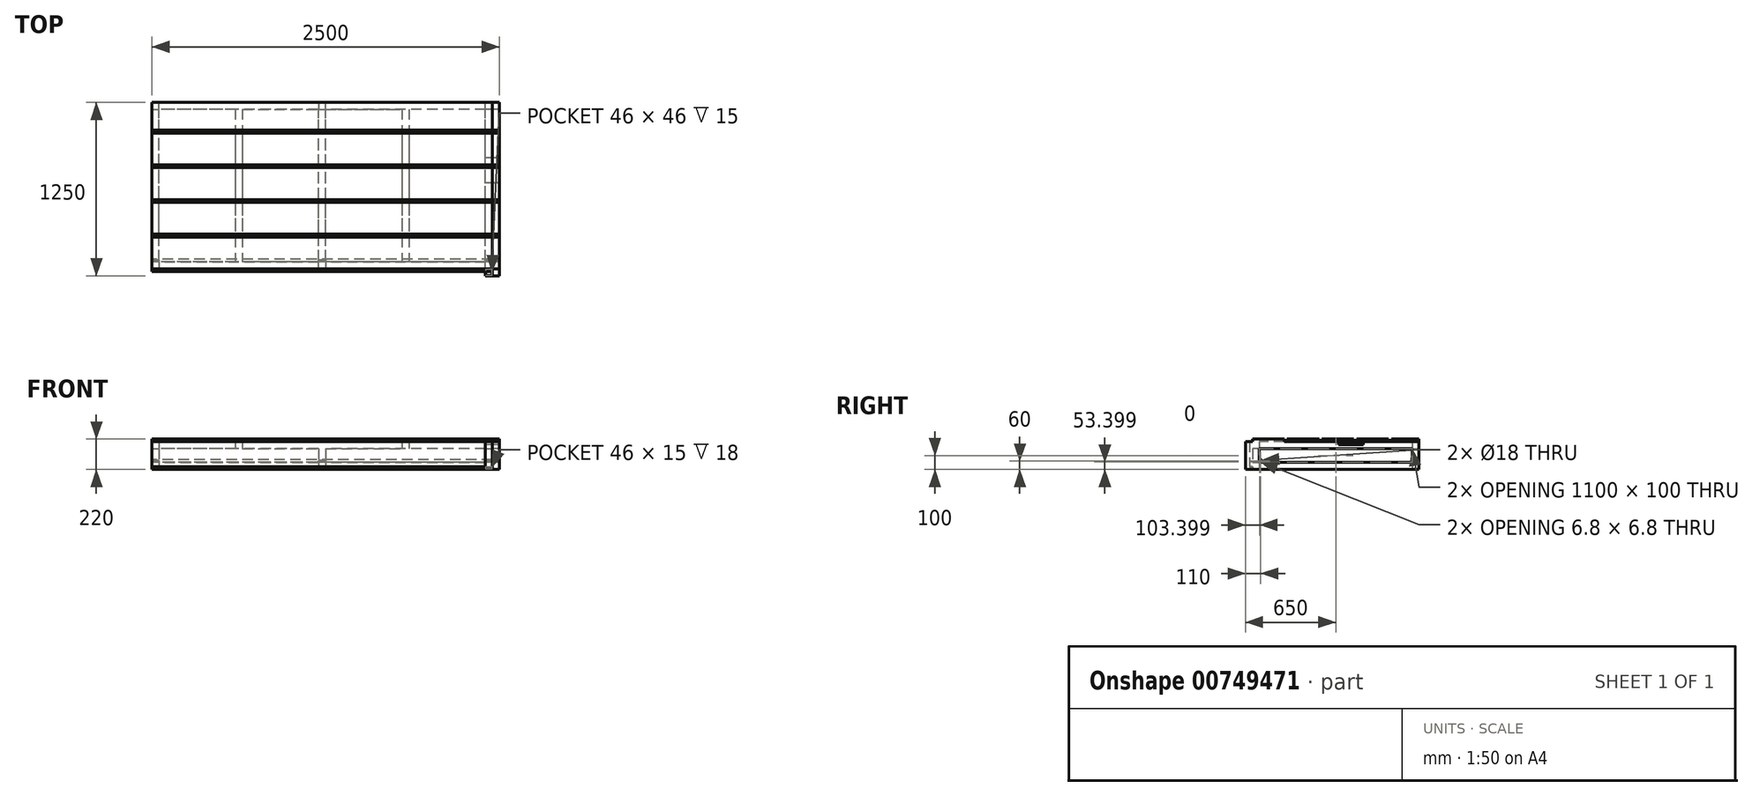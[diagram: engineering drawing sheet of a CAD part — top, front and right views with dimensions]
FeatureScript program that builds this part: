
annotation { "Feature Type Name" : "Feature", "Feature Type Description" : "" }
export const myFeature = defineFeature(function(context is Context, id is Id, definition is map)
    precondition{}
    {
        {
            var Q0;
            Q0=qCreatedBy(makeId("Top.planeOp"),FACE);
            var sketch = newSketch(context, id + "F0", { "sketchPlane" : qUnion([Q0])});
            skLineSegment(sketch, "E0.bottom", {"start": v(1225, -600) * mm, "end": v(-1225, -600) * mm});
            skLineSegment(sketch, "E0.top", {"start": v(1225, 600) * mm, "end": v(-1225, 600) * mm});
            skLineSegment(sketch, "E0.left", {"start": v(1225, -600) * mm, "end": v(1225, 600) * mm});
            skLineSegment(sketch, "E0.right", {"start": v(-1225, -600) * mm, "end": v(-1225, 600) * mm});
            skPoint(sketch, "E0.middle", {"position": v(0, 0) * mm});
            skLineSegment(sketch, "E1.0", {"start": v(1225, 550) * mm, "end": v(-1225, 550) * mm});
            skLineSegment(sketch, "E2.0", {"start": v(1227.5, -600) * mm, "end": v(1227.5, 600) * mm});
            skLineSegment(sketch, "E3.0", {"start": v(1175, -600) * mm, "end": v(1175, 600) * mm});
            skLineSegment(sketch, "E4.0", {"start": v(1225, -550) * mm, "end": v(-1225, -550) * mm});
            skLineSegment(sketch, "E5.0", {"start": v(-1175, -600) * mm, "end": v(-1175, 600) * mm});
            skLineSegment(sketch, "E6", {"start": v(0, 0) * mm, "end": v(0, 550) * mm});
            skLineSegment(sketch, "E7", {"start": v(0, 0) * mm, "end": v(0, -550) * mm});
            skLineSegment(sketch, "E8.0", {"start": v(25, 0) * mm, "end": v(25, 550) * mm});
            skLineSegment(sketch, "E9.0", {"start": v(-25, 0) * mm, "end": v(-25, 550) * mm});
            skLineSegment(sketch, "E10.0", {"start": v(-25, 0) * mm, "end": v(-25, -550) * mm});
            skLineSegment(sketch, "E11.0", {"start": v(25, 0) * mm, "end": v(25, -550) * mm});
            skSolve(sketch);
        }
        {
            var Q0;
            Q0=qSketchRegion(id+"F0",true);
            var Q1;
            {var subQ1=sQuery(id+"F0.wireOp",EDGE,"E6");Q1=makeQuery(id+"F0.imprint","IMPRINT",FACE,{"disambiguationData":[TD([[makeQuery(id+"F0.imprint","IMPRINT",EDGE,{"derivedFrom":subQ1}),-1.0]])]});}
            var Q2;
            {var subQ3=sQuery(id+"F0.wireOp",EDGE,"E6");Q2=makeQuery(id+"F0.imprint","IMPRINT",FACE,{"disambiguationData":[TD([[makeQuery(id+"F0.imprint","IMPRINT",EDGE,{"derivedFrom":subQ3}),1.0]])]});}
            extrude(context, id + "F1", {"entities" : qUnion([Q0, Q1, Q2]), "depth" : 50 * mm, "offsetDistance" : 25 * mm});
        }
        {
            var Q0;
            Q0=makeQuery(id+"F1.opExtrude","CAP_FACE",FACE,{"disambiguationData":[OSD([sQuery(id+"F0.wireOp",EDGE,"E0.bottom"),sQuery(id+"F0.wireOp",EDGE,"E0.top"),sQuery(id+"F0.wireOp",EDGE,"E0.left"),sQuery(id+"F0.wireOp",EDGE,"E0.right"),sQuery(id+"F0.wireOp",EDGE,"E1.0"),sQuery(id+"F0.wireOp",EDGE,"E3.0"),sQuery(id+"F0.wireOp",EDGE,"E4.0"),sQuery(id+"F0.wireOp",EDGE,"E5.0"),sQuery(id+"F0.wireOp",EDGE,"E8.0"),sQuery(id+"F0.wireOp",EDGE,"E9.0"),sQuery(id+"F0.wireOp",EDGE,"E10.0"),sQuery(id+"F0.wireOp",EDGE,"E11.0")])],"isStart":false});
            var sketch = newSketch(context, id + "F2", { "sketchPlane" : qUnion([Q0])});
            skLineSegment(sketch, "E12", {"start": v(-25, 550) * mm, "end": v(25, 550) * mm});
            skLineSegment(sketch, "E13", {"start": v(25, 550) * mm, "end": v(25, 600) * mm});
            skLineSegment(sketch, "E14", {"start": v(25, 600) * mm, "end": v(-25, 600) * mm});
            skLineSegment(sketch, "E15", {"start": v(-25, 600) * mm, "end": v(-25, 550) * mm});
            skLineSegment(sketch, "E16", {"start": v(-1175, 550) * mm, "end": v(-1175, 600) * mm});
            skLineSegment(sketch, "E17", {"start": v(-1175, 600) * mm, "end": v(-1225, 600) * mm});
            skLineSegment(sketch, "E18", {"start": v(-1225, 600) * mm, "end": v(-1225, 550) * mm});
            skLineSegment(sketch, "E19", {"start": v(-1225, 550) * mm, "end": v(-1175, 550) * mm});
            skLineSegment(sketch, "E20", {"start": v(-1175, -550) * mm, "end": v(-1175, -600) * mm});
            skLineSegment(sketch, "E21", {"start": v(-1175, -600) * mm, "end": v(-1225, -600) * mm});
            skLineSegment(sketch, "E22", {"start": v(-1225, -600) * mm, "end": v(-1225, -550) * mm});
            skLineSegment(sketch, "E23", {"start": v(-1225, -550) * mm, "end": v(-1175, -550) * mm});
            skLineSegment(sketch, "E24", {"start": v(-25, -550) * mm, "end": v(25, -550) * mm});
            skLineSegment(sketch, "E25", {"start": v(25, -550) * mm, "end": v(25, -600) * mm});
            skLineSegment(sketch, "E26", {"start": v(25, -600) * mm, "end": v(-25, -600) * mm});
            skPoint(sketch, "E26.endSnap0", {"position": v(0, -600) * mm});
            skLineSegment(sketch, "E27", {"start": v(-25, -600) * mm, "end": v(-25, -550) * mm});
            skLineSegment(sketch, "E28", {"start": v(1175, -550) * mm, "end": v(1225, -550) * mm});
            skLineSegment(sketch, "E29", {"start": v(1225, -550) * mm, "end": v(1225, -600) * mm});
            skLineSegment(sketch, "E30", {"start": v(1225, -600) * mm, "end": v(1175, -600) * mm});
            skLineSegment(sketch, "E31", {"start": v(1175, -600) * mm, "end": v(1175, -550) * mm});
            skLineSegment(sketch, "E32", {"start": v(1175, 550) * mm, "end": v(1175, 600) * mm});
            skLineSegment(sketch, "E33", {"start": v(1175, 600) * mm, "end": v(1225, 600) * mm});
            skLineSegment(sketch, "E34", {"start": v(1225, 600) * mm, "end": v(1225, 550) * mm});
            skLineSegment(sketch, "E35", {"start": v(1225, 550) * mm, "end": v(1175, 550) * mm});
            skSolve(sketch);
        }
        {
            var Q0;
            Q0=qSketchRegion(id+"F2",true);
            extrude(context, id + "F3", {"entities" : qUnion([Q0]), "operationType" : NewBodyOperationType.ADD, "depth" : 100 * mm, "offsetDistance" : 25 * mm});
        }
        {
            var Q0;
            Q0=makeQuery(id+"F3.opExtrude","CAP_FACE",FACE,{"disambiguationData":[OSD([sQuery(id+"F2.wireOp",EDGE,"E12"),sQuery(id+"F2.wireOp",EDGE,"E13"),sQuery(id+"F2.wireOp",EDGE,"E14"),sQuery(id+"F2.wireOp",EDGE,"E15")])],"isStart":false});
            var sketch = newSketch(context, id + "F4", { "sketchPlane" : qUnion([Q0])});
            skLineSegment(sketch, "E36.bottom", {"start": v(-1225, 600) * mm, "end": v(1225, 600) * mm});
            skLineSegment(sketch, "E36.top", {"start": v(-1225, -600) * mm, "end": v(1225, -600) * mm});
            skLineSegment(sketch, "E36.left", {"start": v(-1225, 600) * mm, "end": v(-1225, -600) * mm});
            skLineSegment(sketch, "E36.right", {"start": v(1225, 600) * mm, "end": v(1225, -600) * mm});
            skLineSegment(sketch, "E37.bottom", {"start": v(1175, -550) * mm, "end": v(-1175, -550) * mm});
            skLineSegment(sketch, "E37.top", {"start": v(1175, 550) * mm, "end": v(-1175, 550) * mm});
            skLineSegment(sketch, "E37.left", {"start": v(1175, -550) * mm, "end": v(1175, 550) * mm});
            skLineSegment(sketch, "E37.right", {"start": v(-1175, -550) * mm, "end": v(-1175, 550) * mm});
            skLineSegment(sketch, "E38.bottom", {"start": v(-25, 550) * mm, "end": v(25, 550) * mm});
            skLineSegment(sketch, "E38.top", {"start": v(-25, -550) * mm, "end": v(25, -550) * mm});
            skLineSegment(sketch, "E38.left", {"start": v(-25, 550) * mm, "end": v(-25, -550) * mm});
            skLineSegment(sketch, "E38.right", {"start": v(25, 550) * mm, "end": v(25, -550) * mm});
            skLineSegment(sketch, "E39", {"start": v(-25, 550) * mm, "end": v(-1175, 550) * mm});
            skLineSegment(sketch, "E40", {"start": v(-600, 550) * mm, "end": v(-600, -550) * mm});
            skLineSegment(sketch, "E41.0", {"start": v(-625, 550) * mm, "end": v(-625, -550) * mm});
            skLineSegment(sketch, "E42.0", {"start": v(-575, 550) * mm, "end": v(-575, -550) * mm});
            skLineSegment(sketch, "E43", {"start": v(25, 550) * mm, "end": v(1175, 550) * mm});
            skLineSegment(sketch, "E44", {"start": v(600, 550) * mm, "end": v(600, -550) * mm});
            skLineSegment(sketch, "E45.0", {"start": v(575, 550) * mm, "end": v(575, -550) * mm});
            skLineSegment(sketch, "E46.0", {"start": v(625, 550) * mm, "end": v(625, -550) * mm});
            skSolve(sketch);
        }
        {
            var Q0;
            Q0=qSketchRegion(id+"F4",true);
            var Q1;
            {var subQ0=sQuery(id+"F4.wireOp",EDGE,"E40");Q1=makeQuery(id+"F4.imprint","IMPRINT",FACE,{"disambiguationData":[TD([[makeQuery(id+"F4.imprint","IMPRINT",EDGE,{"derivedFrom":subQ0}),1.0]])]});}
            var Q2;
            {var subQ0=sQuery(id+"F4.wireOp",EDGE,"E40");Q2=makeQuery(id+"F4.imprint","IMPRINT",FACE,{"disambiguationData":[TD([[makeQuery(id+"F4.imprint","IMPRINT",EDGE,{"derivedFrom":subQ0}),-1.0]])]});}
            var Q3;
            {var subQ0=sQuery(id+"F4.wireOp",EDGE,"E44");Q3=makeQuery(id+"F4.imprint","IMPRINT",FACE,{"disambiguationData":[TD([[makeQuery(id+"F4.imprint","IMPRINT",EDGE,{"derivedFrom":subQ0}),1.0]])]});}
            var Q4;
            {var subQ0=sQuery(id+"F4.wireOp",EDGE,"E44");Q4=makeQuery(id+"F4.imprint","IMPRINT",FACE,{"disambiguationData":[TD([[makeQuery(id+"F4.imprint","IMPRINT",EDGE,{"derivedFrom":subQ0}),-1.0]])]});}
            var Q5;
            Q5=makeQuery(id+"F4.imprint","IMPRINT",FACE,{"disambiguationData":[TD([[makeQuery(id+"F4.imprint","IMPRINT",EDGE,{"derivedFrom":sQuery(id+"F4.wireOp",EDGE,"E38.bottom")}),-1.0]])]});
            extrude(context, id + "F5", {"entities" : qUnion([Q0, Q1, Q2, Q3, Q4, Q5]), "operationType" : NewBodyOperationType.ADD, "depth" : 50 * mm, "offsetDistance" : 25 * mm});
        }
        {
            var Q0;
            Q0=makeQuery(id+"F5.boolean.opBoolean","MERGE",FACE,{"derivedFrom":[makeQuery(id+"F3.boolean.opBoolean","MERGE",FACE,{"derivedFrom":[makeQuery(id+"F1.opExtrude","SWEPT_FACE",FACE,{"disambiguationData":[OSD([sQuery(id+"F0.wireOp",EDGE,"E0.right")])]}),makeQuery(id+"F3.opExtrude","SWEPT_FACE",FACE,{"disambiguationData":[OSD([sQuery(id+"F2.wireOp",EDGE,"E18")])]}),makeQuery(id+"F3.opExtrude","SWEPT_FACE",FACE,{"disambiguationData":[OSD([sQuery(id+"F2.wireOp",EDGE,"E22")])]})]}),makeQuery(id+"F5.opExtrude","SWEPT_FACE",FACE,{"disambiguationData":[OSD([sQuery(id+"F4.wireOp",EDGE,"E36.left")])]})]});
            var sketch = newSketch(context, id + "F6", { "sketchPlane" : qUnion([Q0])});
            skLineSegment(sketch, "E47", {"start": v(550, 50) * mm, "end": v(550, 60) * mm});
            skLineSegment(sketch, "E48", {"start": v(550, 60) * mm, "end": v(540, 60) * mm});
            skCircle(sketch, "E49", {"center": v(540, 60) * mm, "radius": 10.5 * mm});
            skCircle(sketch, "E50", {"center": v(540, 60) * mm, "radius": 9 * mm});
            skSolve(sketch);
        }
        {
            var Q0;
            Q0=qSketchRegion(id+"F6",true);
            extrude(context, id + "F7", {"entities" : qUnion([Q0]), "operationType" : NewBodyOperationType.ADD, "oppositeDirection" : true, "depth" : 2450 * mm, "offsetDistance" : 25 * mm});
        }
        {
            var Q0;
            Q0=makeQuery(id+"F5.boolean.opBoolean","MERGE",FACE,{"derivedFrom":[makeQuery(id+"F3.boolean.opBoolean","MERGE",FACE,{"derivedFrom":[makeQuery(id+"F1.opExtrude","SWEPT_FACE",FACE,{"disambiguationData":[OSD([sQuery(id+"F0.wireOp",EDGE,"E0.bottom")])]}),makeQuery(id+"F3.opExtrude","SWEPT_FACE",FACE,{"disambiguationData":[OSD([sQuery(id+"F2.wireOp",EDGE,"E21")])]}),makeQuery(id+"F3.opExtrude","SWEPT_FACE",FACE,{"disambiguationData":[OSD([sQuery(id+"F2.wireOp",EDGE,"E26")])]}),makeQuery(id+"F3.opExtrude","SWEPT_FACE",FACE,{"disambiguationData":[OSD([sQuery(id+"F2.wireOp",EDGE,"E30")])]})]}),makeQuery(id+"F5.opExtrude","SWEPT_FACE",FACE,{"disambiguationData":[OSD([sQuery(id+"F4.wireOp",EDGE,"E36.top")])]})]});
            var sketch = newSketch(context, id + "F8", { "sketchPlane" : qUnion([Q0])});
            skLineSegment(sketch, "E51.bottom", {"start": v(1225, 200) * mm, "end": v(-1275, 200) * mm});
            skLineSegment(sketch, "E51.top", {"start": v(1225, 20) * mm, "end": v(-1275, 20) * mm});
            skLineSegment(sketch, "E51.left", {"start": v(1225, 200) * mm, "end": v(1225, 20) * mm});
            skLineSegment(sketch, "E51.right", {"start": v(-1275, 200) * mm, "end": v(-1275, 20) * mm});
            skLineSegment(sketch, "E52", {"start": v(-1225, 200) * mm, "end": v(-1275, 200) * mm});
            skSolve(sketch);
        }
        {
            var Q0;
            Q0=qSketchRegion(id+"F8",true);
            extrude(context, id + "F9", {"entities" : qUnion([Q0]), "depth" : 20 * mm, "offsetDistance" : 25 * mm});
        }
        {
            var Q0;
            Q0=makeQuery(id+"F5.opExtrude","CAP_FACE",FACE,{"disambiguationData":[OSD([sQuery(id+"F4.wireOp",EDGE,"E36.bottom"),sQuery(id+"F4.wireOp",EDGE,"E36.top"),sQuery(id+"F4.wireOp",EDGE,"E36.left"),sQuery(id+"F4.wireOp",EDGE,"E36.right"),sQuery(id+"F4.wireOp",EDGE,"E37.bottom"),sQuery(id+"F4.wireOp",EDGE,"E37.left"),sQuery(id+"F4.wireOp",EDGE,"E37.right"),sQuery(id+"F4.wireOp",EDGE,"E38.left"),sQuery(id+"F4.wireOp",EDGE,"E38.right"),sQuery(id+"F4.wireOp",EDGE,"E39"),sQuery(id+"F4.wireOp",EDGE,"E41.0"),sQuery(id+"F4.wireOp",EDGE,"E42.0"),sQuery(id+"F4.wireOp",EDGE,"E43"),sQuery(id+"F4.wireOp",EDGE,"E45.0"),sQuery(id+"F4.wireOp",EDGE,"E46.0")])],"isStart":false});
            var sketch = newSketch(context, id + "F10", { "sketchPlane" : qUnion([Q0])});
            skLineSegment(sketch, "E53.bottom", {"start": v(1225, 600) * mm, "end": v(-1275, 600) * mm});
            skLineSegment(sketch, "E53.top", {"start": v(1225, -600) * mm, "end": v(-1275, -600) * mm});
            skLineSegment(sketch, "E53.left", {"start": v(1225, 600) * mm, "end": v(1225, -600) * mm});
            skLineSegment(sketch, "E53.right", {"start": v(-1275, 600) * mm, "end": v(-1275, -600) * mm});
            skSolve(sketch);
        }
        {
            var Q0;
            Q0=qSketchRegion(id+"F10",true);
            extrude(context, id + "F11", {"entities" : qUnion([Q0]), "depth" : 20 * mm, "offsetDistance" : 25 * mm});
        }
        {
            var Q0;
            Q0=makeQuery(id+"F9.opExtrude","SWEPT_FACE",FACE,{"disambiguationData":[OSD([sQuery(id+"F8.wireOp",EDGE,"E51.right")])]});
            extrude(context, id + "F12", {"entities" : qUnion([Q0]), "operationType" : NewBodyOperationType.REMOVE, "oppositeDirection" : true, "depth" : 110 * mm, "offsetDistance" : 25 * mm});
        }
        {
            var Q0;
            Q0=makeQuery(id+"F11.opExtrude","SWEPT_FACE",FACE,{"disambiguationData":[OSD([sQuery(id+"F10.wireOp",EDGE,"E53.right")])]});
            var sketch = newSketch(context, id + "F13", { "sketchPlane" : qUnion([Q0])});
            skLineSegment(sketch, "E54.bottom", {"start": v(600, 200) * mm, "end": v(620.46, 200) * mm});
            skLineSegment(sketch, "E54.top", {"start": v(600, 220) * mm, "end": v(620.46, 220) * mm});
            skLineSegment(sketch, "E54.left", {"start": v(600, 200) * mm, "end": v(600, 220) * mm});
            skLineSegment(sketch, "E54.right", {"start": v(620.46, 200) * mm, "end": v(620.46, 220) * mm});
            skLineSegment(sketch, "E55.1.0.0", {"start": v(350, 220) * mm, "end": v(370.46, 220) * mm});
            skLineSegment(sketch, "E55.1.0.1", {"start": v(370.46, 200) * mm, "end": v(370.46, 220) * mm});
            skLineSegment(sketch, "E55.1.0.2", {"start": v(350, 200) * mm, "end": v(370.46, 200) * mm});
            skLineSegment(sketch, "E55.1.0.3", {"start": v(350, 200) * mm, "end": v(350, 220) * mm});
            skLineSegment(sketch, "E55.2.0.0", {"start": v(100, 220) * mm, "end": v(120.46, 220) * mm});
            skLineSegment(sketch, "E55.2.0.1", {"start": v(120.46, 200) * mm, "end": v(120.46, 220) * mm});
            skLineSegment(sketch, "E55.2.0.2", {"start": v(100, 200) * mm, "end": v(120.46, 200) * mm});
            skLineSegment(sketch, "E55.2.0.3", {"start": v(100, 200) * mm, "end": v(100, 220) * mm});
            skLineSegment(sketch, "E55.3.0.0", {"start": v(-150, 220) * mm, "end": v(-129.54, 220) * mm});
            skLineSegment(sketch, "E55.3.0.1", {"start": v(-129.54, 200) * mm, "end": v(-129.54, 220) * mm});
            skLineSegment(sketch, "E55.3.0.2", {"start": v(-150, 200) * mm, "end": v(-129.54, 200) * mm});
            skLineSegment(sketch, "E55.3.0.3", {"start": v(-150, 200) * mm, "end": v(-150, 220) * mm});
            skLineSegment(sketch, "E55.4.0.0", {"start": v(-400, 220) * mm, "end": v(-379.54, 220) * mm});
            skLineSegment(sketch, "E55.4.0.1", {"start": v(-379.54, 200) * mm, "end": v(-379.54, 220) * mm});
            skLineSegment(sketch, "E55.4.0.2", {"start": v(-400, 200) * mm, "end": v(-379.54, 200) * mm});
            skLineSegment(sketch, "E55.4.0.3", {"start": v(-400, 200) * mm, "end": v(-400, 220) * mm});
            skLineSegment(sketch, "E55.direction1", {"start": v(600, 200) * mm, "end": v(350, 200) * mm, "construction": true});
            skSolve(sketch);
        }
        {
            var Q0;
            Q0=qSketchRegion(id+"F13",true);
            var Q1;
            Q1=makeQuery(id+"F11.opExtrude","SWEPT_FACE",FACE,{"disambiguationData":[OSD([sQuery(id+"F10.wireOp",EDGE,"E53.left")])]});
            extrude(context, id + "F14", {"entities" : qUnion([Q0]), "operationType" : NewBodyOperationType.REMOVE, "endBound" : BoundingType.UP_TO_SURFACE, "oppositeDirection" : true, "depth" : 25 * mm, "endBoundEntityFace" : qUnion([Q1]), "offsetDistance" : 25 * mm});
        }
        {
            var Q0;
            Q0=makeQuery(id+"F12.boolean.opBoolean","COPY",FACE,{"derivedFrom":makeQuery(id+"F12.opExtrude","CAP_FACE",FACE,{"disambiguationData":[OSD([sQuery(id+"F8.wireOp",EDGE,"E51.right")])],"isStart":false})});
            var Q1;
            Q1=makeQuery(id+"F5.boolean.opBoolean","MERGE",FACE,{"derivedFrom":[makeQuery(id+"F3.boolean.opBoolean","MERGE",FACE,{"derivedFrom":[makeQuery(id+"F1.opExtrude","SWEPT_FACE",FACE,{"disambiguationData":[OSD([sQuery(id+"F0.wireOp",EDGE,"E0.right")])]}),makeQuery(id+"F3.opExtrude","SWEPT_FACE",FACE,{"disambiguationData":[OSD([sQuery(id+"F2.wireOp",EDGE,"E18")])]}),makeQuery(id+"F3.opExtrude","SWEPT_FACE",FACE,{"disambiguationData":[OSD([sQuery(id+"F2.wireOp",EDGE,"E22")])]})]}),makeQuery(id+"F5.opExtrude","SWEPT_FACE",FACE,{"disambiguationData":[OSD([sQuery(id+"F4.wireOp",EDGE,"E36.left")])]})]});
            extrude(context, id + "F15", {"entities" : qUnion([Q0]), "endBound" : BoundingType.UP_TO_SURFACE, "depth" : 25 * mm, "endBoundEntityFace" : qUnion([Q1]), "offsetDistance" : 25 * mm});
        }
        {
            var Q0;
            Q0=makeQuery(id+"F9.opExtrude","SWEPT_BODY",BODY,{"disambiguationData":[OSD([sQuery(id+"F8.wireOp",EDGE,"E51.bottom"),sQuery(id+"F8.wireOp",EDGE,"E51.top"),sQuery(id+"F8.wireOp",EDGE,"E51.left"),sQuery(id+"F8.wireOp",EDGE,"E51.right"),sQuery(id+"F8.wireOp",EDGE,"E52")])]});
            var Q1;
            Q1=makeQuery(id+"F15.opExtrude","SWEPT_BODY",BODY,{"disambiguationData":[OSD([sQuery(id+"F8.wireOp",EDGE,"E51.right")])]});
            booleanBodies(context, id + "F16", {"operationType" : BooleanOperationType.UNION, "tools" : qUnion([Q0, Q1])});
        }
        {
            var Q0;
            Q0=makeQuery(id+"F11.opExtrude","SWEPT_FACE",FACE,{"disambiguationData":[OSD([sQuery(id+"F10.wireOp",EDGE,"E53.top")])]});
            var sketch = newSketch(context, id + "F17", { "sketchPlane" : qUnion([Q0])});
            skLineSegment(sketch, "E56.bottom", {"start": v(-1225, 200) * mm, "end": v(-1275, 200) * mm});
            skLineSegment(sketch, "E56.top", {"start": v(-1225, 220) * mm, "end": v(-1275, 220) * mm});
            skLineSegment(sketch, "E56.left", {"start": v(-1225, 200) * mm, "end": v(-1225, 220) * mm});
            skLineSegment(sketch, "E56.right", {"start": v(-1275, 200) * mm, "end": v(-1275, 220) * mm});
            skSolve(sketch);
        }
        {
            var Q0;
            Q0 = qSketchRegion(id + "F17", true);
            extrude(context, id + "F18", {"entities" : qUnion([Q0]), "operationType" : NewBodyOperationType.REMOVE, "endBound" : BoundingType.THROUGH_ALL, "oppositeDirection" : true, "depth" : 25 * mm, "offsetDistance" : 25 * mm});
        }
        {
            var Q0;
            {var subQ0=sQuery(id+"F8.wireOp",EDGE,"E51.right");Q0=makeQuery(id+"F16.opBoolean","MERGE",FACE,{"derivedFrom":[makeQuery(id+"F9.opExtrude","CAP_FACE",FACE,{"disambiguationData":[OSD([sQuery(id+"F8.wireOp",EDGE,"E51.bottom"),sQuery(id+"F8.wireOp",EDGE,"E51.top"),sQuery(id+"F8.wireOp",EDGE,"E51.left"),subQ0,sQuery(id+"F8.wireOp",EDGE,"E52")])],"isStart":false}),makeQuery(id+"F15.opExtrude","SWEPT_FACE",FACE,{"disambiguationData":[OSD([subQ0]),TDD([makeQuery(id+"F12.boolean.opBoolean","COPY",EDGE,{"derivedFrom":makeQuery(id+"F12.opExtrude","CAP_EDGE",EDGE,{"disambiguationData":[OSD([subQ0]),TDD([makeQuery(id+"F9.opExtrude","CAP_EDGE",EDGE,{"disambiguationData":[OSD([subQ0])],"isStart":false})])],"isStart":false})})])]})]});}
            var sketch = newSketch(context, id + "F19", { "sketchPlane" : qUnion([Q0])});
            skLineSegment(sketch, "E57.bottom", {"start": v(1225, 200) * mm, "end": v(1165, 200) * mm});
            skLineSegment(sketch, "E57.top", {"start": v(1225, 20) * mm, "end": v(1165, 20) * mm});
            skLineSegment(sketch, "E57.left", {"start": v(1225, 200) * mm, "end": v(1225, 20) * mm});
            skLineSegment(sketch, "E57.right", {"start": v(1165, 200) * mm, "end": v(1165, 20) * mm});
            skSolve(sketch);
        }
        {
            var Q0;
            Q0 = qSketchRegion(id + "F19", true);
            extrude(context, id + "F20", {"entities" : qUnion([Q0]), "operationType" : NewBodyOperationType.REMOVE, "oppositeDirection" : true, "depth" : 20 * mm, "offsetDistance" : 25 * mm});
        }
        {
            var Q0;
            Q0=makeQuery(id+"F1.opExtrude","CAP_FACE",FACE,{"disambiguationData":[OSD([sQuery(id+"F0.wireOp",EDGE,"E0.bottom"),sQuery(id+"F0.wireOp",EDGE,"E0.top"),sQuery(id+"F0.wireOp",EDGE,"E0.left"),sQuery(id+"F0.wireOp",EDGE,"E0.right"),sQuery(id+"F0.wireOp",EDGE,"E1.0"),sQuery(id+"F0.wireOp",EDGE,"E3.0"),sQuery(id+"F0.wireOp",EDGE,"E4.0"),sQuery(id+"F0.wireOp",EDGE,"E5.0"),sQuery(id+"F0.wireOp",EDGE,"E8.0"),sQuery(id+"F0.wireOp",EDGE,"E9.0"),sQuery(id+"F0.wireOp",EDGE,"E10.0"),sQuery(id+"F0.wireOp",EDGE,"E11.0")])],"isStart":true});
            var sketch = newSketch(context, id + "F21", { "sketchPlane" : qUnion([Q0])});
            skLineSegment(sketch, "E58.bottom", {"start": v(1225, 600) * mm, "end": v(1175, 600) * mm});
            skLineSegment(sketch, "E58.top", {"start": v(1225, 650) * mm, "end": v(1175, 650) * mm});
            skLineSegment(sketch, "E58.left", {"start": v(1225, 600) * mm, "end": v(1225, 650) * mm});
            skLineSegment(sketch, "E58.right", {"start": v(1175, 600) * mm, "end": v(1175, 650) * mm});
            skSolve(sketch);
        }
        {
            var Q0;
            Q0 = qSketchRegion(id + "F21", true);
            extrude(context, id + "F22", {"entities" : qUnion([Q0]), "operationType" : NewBodyOperationType.ADD, "oppositeDirection" : true, "depth" : 5 * mm, "offsetDistance" : 25 * mm});
        }
        {
            var Q0;
            Q0=makeQuery(id+"F22.opExtrude","CAP_FACE",FACE,{"disambiguationData":[OSD([sQuery(id+"F21.wireOp",EDGE,"E58.bottom"),sQuery(id+"F21.wireOp",EDGE,"E58.top"),sQuery(id+"F21.wireOp",EDGE,"E58.left"),sQuery(id+"F21.wireOp",EDGE,"E58.right")])],"isStart":false});
            var sketch = newSketch(context, id + "F23", { "sketchPlane" : qUnion([Q0])});
            skLineSegment(sketch, "E59.bottom", {"start": v(1175, -600) * mm, "end": v(1177, -600) * mm});
            skLineSegment(sketch, "E59.top", {"start": v(1175, -602) * mm, "end": v(1177, -602) * mm});
            skLineSegment(sketch, "E59.left", {"start": v(1175, -600) * mm, "end": v(1175, -602) * mm});
            skLineSegment(sketch, "E59.right", {"start": v(1177, -600) * mm, "end": v(1177, -602) * mm});
            skLineSegment(sketch, "E60.bottom", {"start": v(1175, -600) * mm, "end": v(1225, -600) * mm});
            skLineSegment(sketch, "E60.top", {"start": v(1175, -650) * mm, "end": v(1225, -650) * mm});
            skLineSegment(sketch, "E60.left", {"start": v(1175, -600) * mm, "end": v(1175, -650) * mm});
            skLineSegment(sketch, "E60.right", {"start": v(1225, -600) * mm, "end": v(1225, -650) * mm});
            skLineSegment(sketch, "E61.bottom", {"start": v(1177, -602) * mm, "end": v(1223, -602) * mm});
            skLineSegment(sketch, "E61.top", {"start": v(1177, -648) * mm, "end": v(1223, -648) * mm});
            skLineSegment(sketch, "E61.left", {"start": v(1177, -602) * mm, "end": v(1177, -648) * mm});
            skLineSegment(sketch, "E61.right", {"start": v(1223, -602) * mm, "end": v(1223, -648) * mm});
            skSolve(sketch);
        }
        {
            var Q0;
            {var subQ4=sQuery(id+"F23.wireOp",EDGE,"E59.top");Q0=makeQuery(id+"F23.imprint","IMPRINT",FACE,{"disambiguationData":[TD([[makeQuery(id+"F23.imprint","IMPRINT",EDGE,{"derivedFrom":subQ4}),-1.0]])]});}
            var Q1;
            {var subQ0=sQuery(id+"F23.wireOp",EDGE,"E59.top");Q1=makeQuery(id+"F23.imprint","IMPRINT",FACE,{"disambiguationData":[TD([[makeQuery(id+"F23.imprint","IMPRINT",EDGE,{"derivedFrom":subQ0}),1.0]])]});}
            var Q2;
            {var subQ0=sQuery(id+"F8.wireOp",EDGE,"E52");Q2=makeQuery(id+"F16.opBoolean","MERGE",FACE,{"derivedFrom":[makeQuery(id+"F9.opExtrude","SWEPT_FACE",FACE,{"disambiguationData":[OSD([sQuery(id+"F8.wireOp",EDGE,"E51.bottom"),subQ0])]}),makeQuery(id+"F15.opExtrude","SWEPT_FACE",FACE,{"disambiguationData":[OSD([sQuery(id+"F8.wireOp",EDGE,"E51.right"),subQ0])]})]});}
            extrude(context, id + "F24", {"entities" : qUnion([Q0, Q1]), "operationType" : NewBodyOperationType.ADD, "endBound" : BoundingType.UP_TO_SURFACE, "depth" : 25 * mm, "endBoundEntityFace" : qUnion([Q2]), "offsetDistance" : 25 * mm});
        }
        {
            var Q0;
            {var subQ1=sQuery(id+"F10.wireOp",EDGE,"E53.left");var subQ2=sQuery(id+"F10.wireOp",EDGE,"E53.top");Q0=makeQuery(id+"F14.boolean.opBoolean","SPLIT",FACE,{"disambiguationData":[TD([makeQuery(id+"F11.opExtrude","SWEPT_FACE",FACE,{"disambiguationData":[OSD([subQ2])]})])],"derivedFrom":makeQuery(id+"F11.opExtrude","SWEPT_FACE",FACE,{"disambiguationData":[OSD([subQ1])]})});}
            var Q1;
            {var subQ1=sQuery(id+"F10.wireOp",EDGE,"E53.left");Q1=makeQuery(id+"F14.boolean.opBoolean","SPLIT",FACE,{"disambiguationData":[TD([makeQuery(id+"F14.opExtrude","SWEPT_FACE",FACE,{"disambiguationData":[OSD([sQuery(id+"F13.wireOp",EDGE,"E55.1.0.3")])]})])],"derivedFrom":makeQuery(id+"F11.opExtrude","SWEPT_FACE",FACE,{"disambiguationData":[OSD([subQ1])]})});}
            var Q2;
            {var subQ1=sQuery(id+"F10.wireOp",EDGE,"E53.left");Q2=makeQuery(id+"F14.boolean.opBoolean","SPLIT",FACE,{"disambiguationData":[TD([makeQuery(id+"F14.opExtrude","SWEPT_FACE",FACE,{"disambiguationData":[OSD([sQuery(id+"F13.wireOp",EDGE,"E55.2.0.3")])]})])],"derivedFrom":makeQuery(id+"F11.opExtrude","SWEPT_FACE",FACE,{"disambiguationData":[OSD([subQ1])]})});}
            var Q3;
            {var subQ1=sQuery(id+"F10.wireOp",EDGE,"E53.left");Q3=makeQuery(id+"F14.boolean.opBoolean","SPLIT",FACE,{"disambiguationData":[TD([makeQuery(id+"F14.opExtrude","SWEPT_FACE",FACE,{"disambiguationData":[OSD([sQuery(id+"F13.wireOp",EDGE,"E55.3.0.3")])]})])],"derivedFrom":makeQuery(id+"F11.opExtrude","SWEPT_FACE",FACE,{"disambiguationData":[OSD([subQ1])]})});}
            var Q4;
            {var subQ0=sQuery(id+"F10.wireOp",EDGE,"E53.bottom");var subQ2=sQuery(id+"F10.wireOp",EDGE,"E53.left");Q4=makeQuery(id+"F14.boolean.opBoolean","SPLIT",FACE,{"disambiguationData":[TD([makeQuery(id+"F11.opExtrude","SWEPT_FACE",FACE,{"disambiguationData":[OSD([subQ0])]})])],"derivedFrom":makeQuery(id+"F11.opExtrude","SWEPT_FACE",FACE,{"disambiguationData":[OSD([subQ2])]})});}
            extrude(context, id + "F25", {"entities" : qUnion([Q0, Q1, Q2, Q3, Q4]), "depth" : 50 * mm, "offsetDistance" : 25 * mm});
        }
    });
